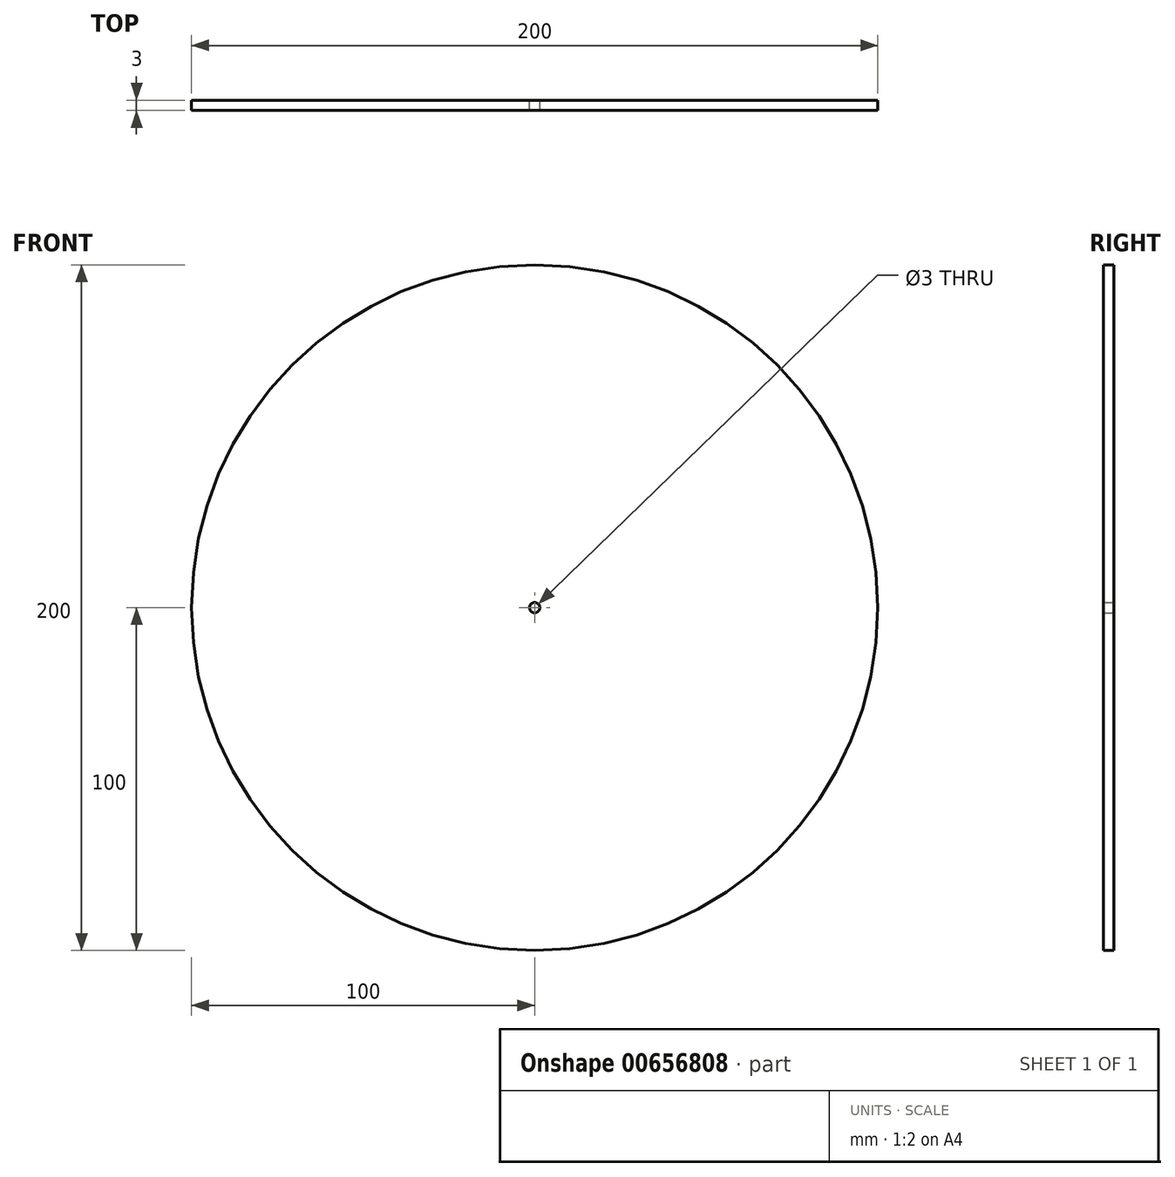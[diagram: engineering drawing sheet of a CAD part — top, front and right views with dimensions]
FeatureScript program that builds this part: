
annotation { "Feature Type Name" : "Feature", "Feature Type Description" : "" }
export const myFeature = defineFeature(function(context is Context, id is Id, definition is map)
    precondition{}
    {
        {
            var Q0;
            Q0=qCreatedBy(makeId("Front.planeOp"),FACE);
            var sketch = newSketch(context, id + "F0", { "sketchPlane" : qUnion([Q0])});
            skCircle(sketch, "E0", {"center": v(0, 0) * mm, "radius": 100 * mm});
            skCircle(sketch, "E1", {"center": v(0, 0) * mm, "radius": 1.5 * mm});
            skSolve(sketch);
        }
        {
            var Q0;
            Q0 = qSketchRegion(id + "F0", true);
            extrude(context, id + "F1", {"entities" : qUnion([Q0]), "depth" : 3 * mm, "offsetDistance" : 25 * mm});
        }
    });
